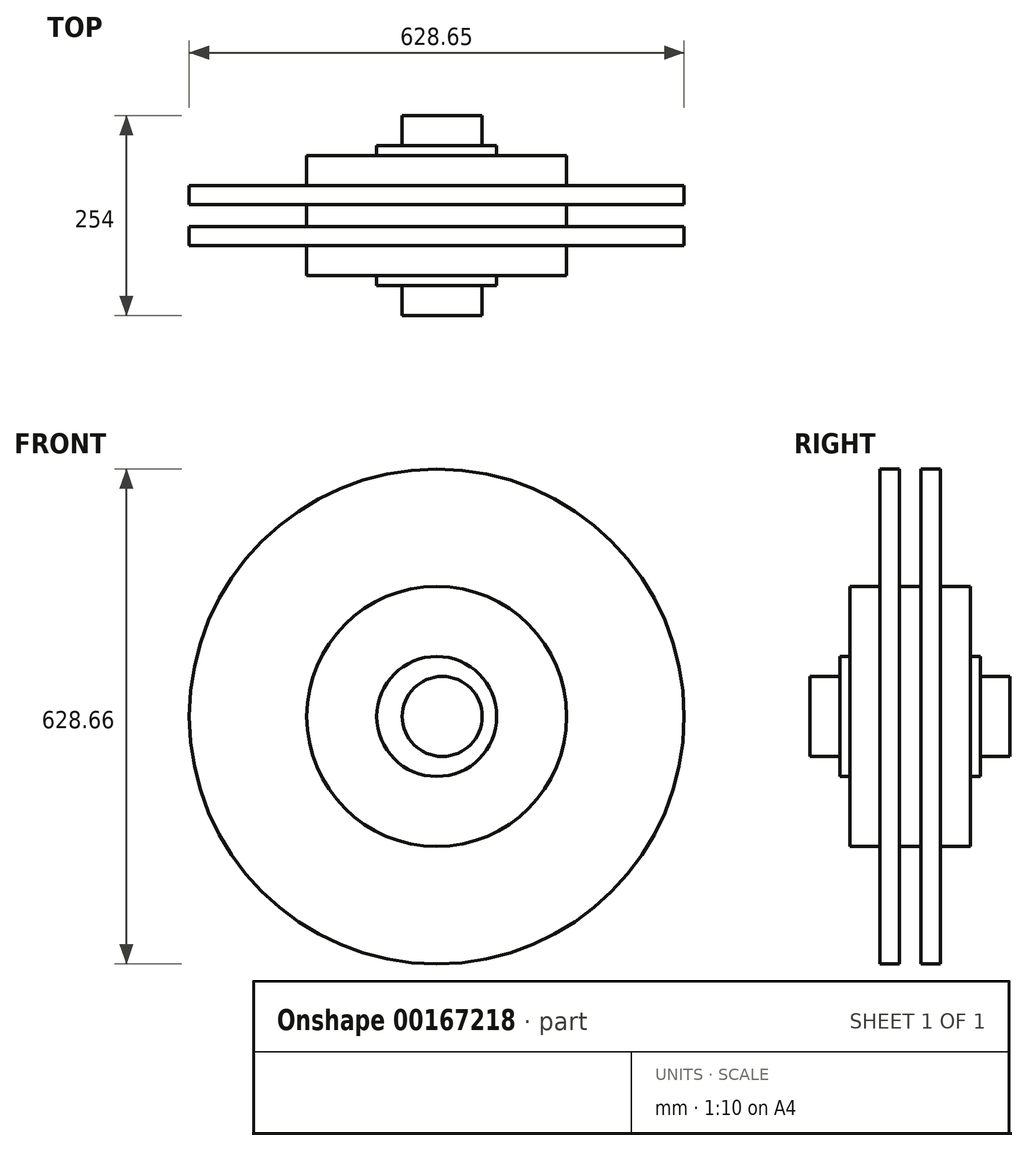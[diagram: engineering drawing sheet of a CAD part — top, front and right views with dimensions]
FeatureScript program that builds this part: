
annotation { "Feature Type Name" : "Feature", "Feature Type Description" : "" }
export const myFeature = defineFeature(function(context is Context, id is Id, definition is map)
    precondition{}
    {
        {
            var Q0;
            Q0=qCreatedBy(makeId("Front.planeOp"),FACE);
            var sketch = newSketch(context, id + "F0", { "sketchPlane" : qUnion([Q0])});
            skCircle(sketch, "E0", {"center": v(0, 0) * mm, "radius": 50.8 * mm});
            skSolve(sketch);
        }
        {
            var Q0;
            Q0 = qSketchRegion(id + "F0", true);
            extrude(context, id + "F1", {"entities" : qUnion([Q0]), "endBound" : BoundingType.SYMMETRIC, "depth" : 254 * mm});
        }
        {
            var Q0;
            Q0=qCreatedBy(makeId("Top.planeOp"),FACE);
            var sketch = newSketch(context, id + "F2", { "sketchPlane" : qUnion([Q0])});
            skLineSegment(sketch, "E1", {"start": v(0, 0) * mm, "end": v(0, -127.05) * mm});
            skLineSegment(sketch, "E2", {"start": v(0, 0) * mm, "end": v(221.17, 0) * mm});
            skLineSegment(sketch, "E3", {"start": v(0, 0) * mm, "end": v(33.66, 0) * mm});
            skLineSegment(sketch, "E4", {"start": v(33.66, 0) * mm, "end": v(33.66, -126.95) * mm});
            skLineSegment(sketch, "E5", {"start": v(-6.98, -106.14) * mm, "end": v(-6.98, 0) * mm});
            skLineSegment(sketch, "E6", {"start": v(69.22, -89) * mm, "end": v(69.22, -76.3) * mm});
            skLineSegment(sketch, "E7", {"start": v(69.22, -76.3) * mm, "end": v(158.12, -76.3) * mm});
            skLineSegment(sketch, "E8", {"start": v(158.12, -76.3) * mm, "end": v(158.12, -38.15) * mm});
            skLineSegment(sketch, "E9", {"start": v(158.12, -38.15) * mm, "end": v(307.35, -38.15) * mm});
            skPoint(sketch, "E9.endSnap0", {"position": v(158.12, -38.15) * mm});
            skLineSegment(sketch, "E10", {"start": v(307.35, -38.15) * mm, "end": v(307.35, -13.85) * mm});
            skLineSegment(sketch, "E11", {"start": v(307.35, -13.85) * mm, "end": v(158.12, -13.85) * mm});
            skLineSegment(sketch, "E12.MirrorCS", {"start": v(33.66, 0) * mm, "end": v(33.66, 126.95) * mm});
            skLineSegment(sketch, "E13.MirrorCS", {"start": v(69.22, 89) * mm, "end": v(69.22, 76.3) * mm});
            skLineSegment(sketch, "E14.MirrorCS", {"start": v(69.22, 76.3) * mm, "end": v(158.12, 76.3) * mm});
            skLineSegment(sketch, "E15.MirrorCS", {"start": v(158.12, 76.3) * mm, "end": v(158.12, 38.15) * mm});
            skLineSegment(sketch, "E16.MirrorCS", {"start": v(158.12, 38.15) * mm, "end": v(307.35, 38.15) * mm});
            skLineSegment(sketch, "E17.MirrorCS", {"start": v(307.35, 13.85) * mm, "end": v(158.12, 13.85) * mm});
            skLineSegment(sketch, "E18.MirrorCS", {"start": v(307.35, 38.15) * mm, "end": v(307.35, 13.85) * mm});
            skLineSegment(sketch, "E19.MirrorCS", {"start": v(-6.98, 106.14) * mm, "end": v(-6.98, 0) * mm});
            skLineSegment(sketch, "E20", {"start": v(69.22, -89) * mm, "end": v(33.66, -89) * mm});
            skLineSegment(sketch, "E21", {"start": v(69.22, 89) * mm, "end": v(33.66, 89) * mm});
            skLineSegment(sketch, "E22.trimOffspring", {"start": v(158.12, -13.85) * mm, "end": v(158.12, 0) * mm});
            skLineSegment(sketch, "E23.trimOffspring", {"start": v(158.12, 13.85) * mm, "end": v(158.12, 0) * mm});
            skPoint(sketch, "E24.orphan", {"position": v(69.22, 0) * mm});
            skSolve(sketch);
        }
        {
            var Q0;
            Q0=makeQuery(id+"F2.imprint","IMPRINT",FACE,{"disambiguationData":[TD([[makeQuery(id+"F2.imprint","IMPRINT",EDGE,{"derivedFrom":sQuery(id+"F2.wireOp",EDGE,"E6")}),1.0]])]});
            var Q1;
            Q1=makeQuery(id+"F2.imprint","IMPRINT",FACE,{"disambiguationData":[TD([[makeQuery(id+"F2.imprint","IMPRINT",EDGE,{"derivedFrom":sQuery(id+"F2.wireOp",EDGE,"E13.MirrorCS")}),-1.0]])]});
            var Q2;
            Q2=sQuery(id+"F2.wireOp",EDGE,"E19.MirrorCS");
            revolve(context, id + "F3", {"operationType" : NewBodyOperationType.ADD, "entities" : qUnion([Q0, Q1]), "axis" : qUnion([Q2]), "revolveType" : RevolveType.FULL});
        }
    });
